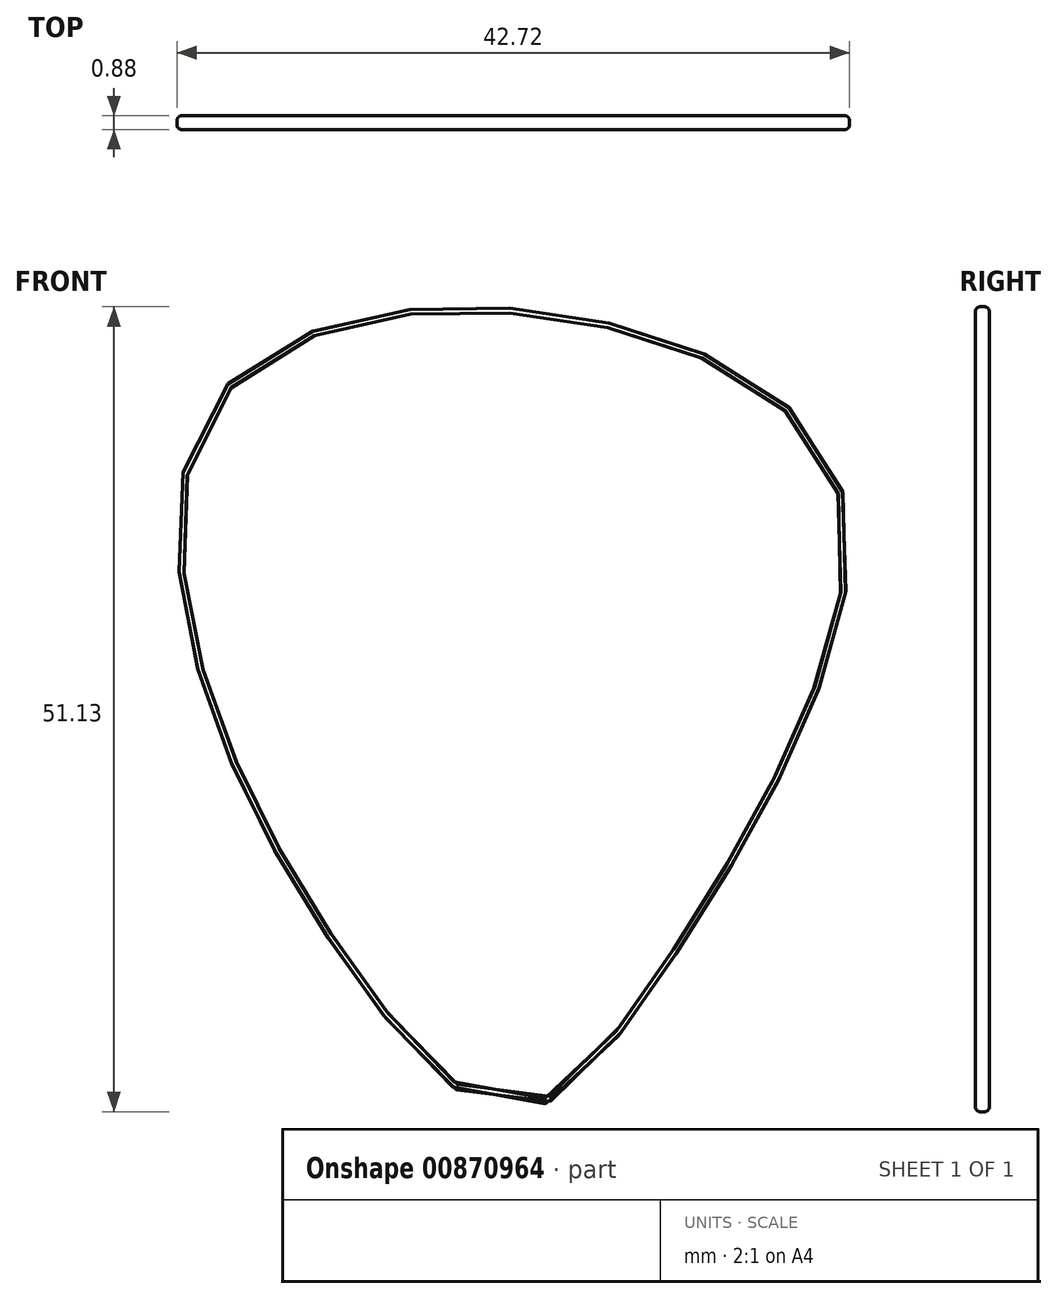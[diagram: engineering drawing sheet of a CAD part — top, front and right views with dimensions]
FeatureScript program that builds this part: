
annotation { "Feature Type Name" : "Feature", "Feature Type Description" : "" }
export const myFeature = defineFeature(function(context is Context, id is Id, definition is map)
    precondition{}
    {
        {
            var Q0;
            Q0=qCreatedBy(makeId("Front.planeOp"),FACE);
            var sketch = newSketch(context, id + "F0", { "sketchPlane" : qUnion([Q0])});
            skFitSpline(sketch, "E0", {"points": [v(0, 22) * mm, v(-18.62, 16.34) * mm, v(-20.04, 0) * mm, v(-10.12, -20.04) * mm, v(0, -29.02) * mm, v(10.2, -19.57) * mm, v(21.06, 10.67) * mm, v(0, 22) * mm]});
            skSolve(sketch);
        }
        {
            var Q0;
            Q0=makeQuery(id+"F0.imprint","IMPRINT",FACE,{"disambiguationData":[TD([[makeQuery(id+"F0.imprint","IMPRINT",EDGE,{"derivedFrom":sQuery(id+"F0.wireOp",EDGE,"E0")}),1.0]])]});
            extrude(context, id + "F1", {"entities" : qUnion([Q0]), "depth" : 0.88 * mm, "offsetDistance" : 25.4 * mm});
        }
        {
            var Q0;
            Q0=makeQuery(id+"F1.opExtrude","CAP_EDGE",EDGE,{"disambiguationData":[OSD([sQuery(id+"F0.wireOp",EDGE,"E0")])],"isStart":false});
            var Q1;
            Q1=makeQuery(id+"F1.opExtrude","CAP_EDGE",EDGE,{"disambiguationData":[OSD([sQuery(id+"F0.wireOp",EDGE,"E0")])],"isStart":true});
            fillet(context, id + "F2", {"entities" : qUnion([Q0, Q1]), "radius" : 0.3 * mm, "tangentPropagation" : true, "allowEdgeOverflow" : false});
        }
    });
